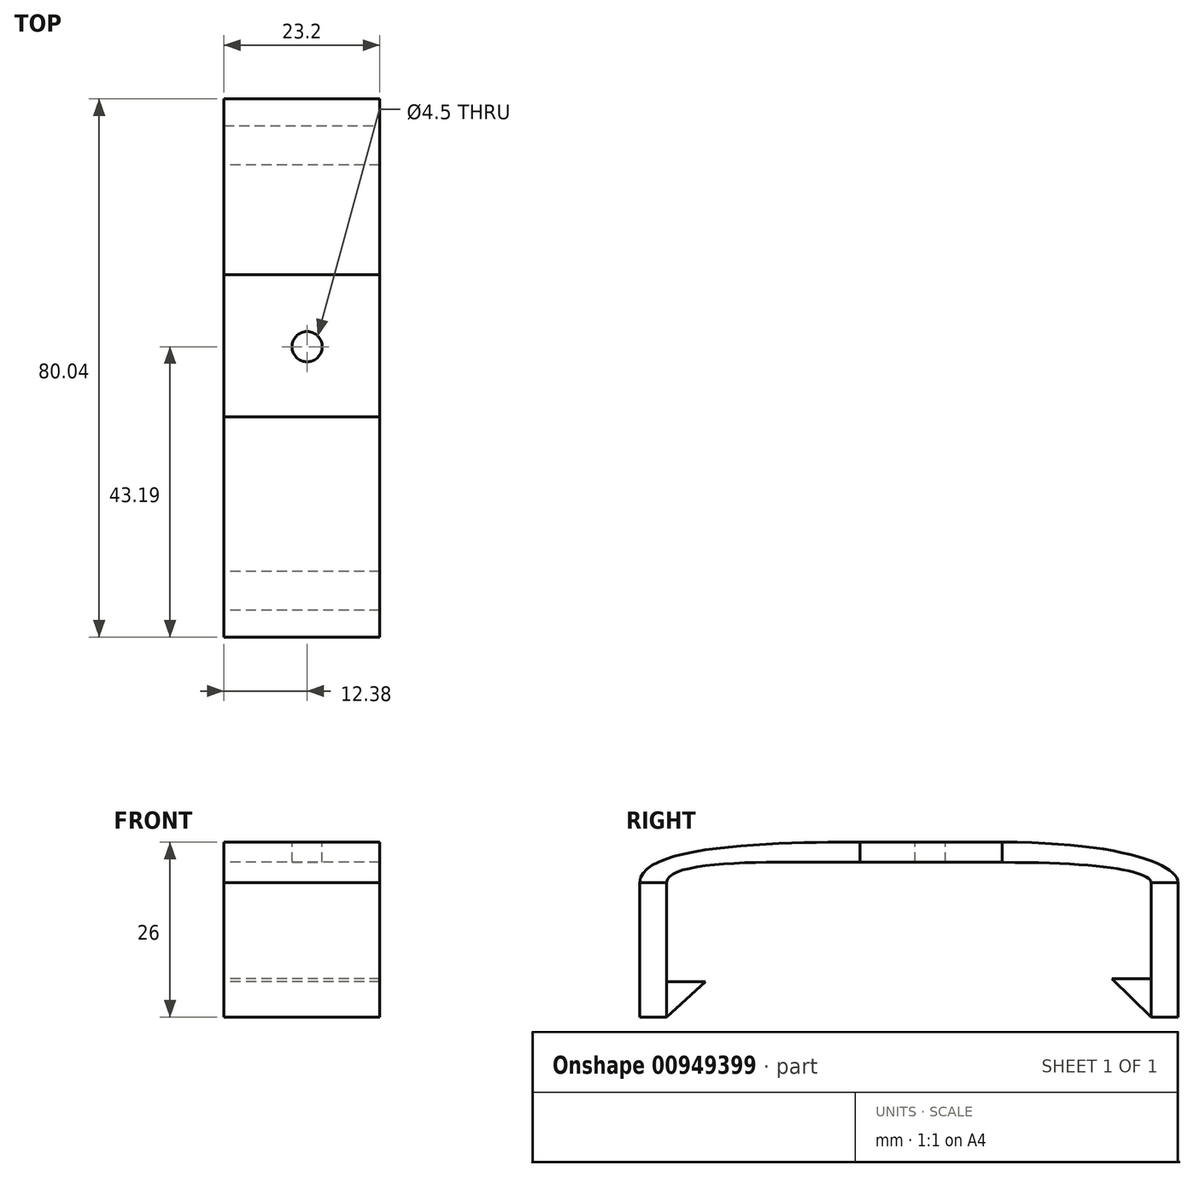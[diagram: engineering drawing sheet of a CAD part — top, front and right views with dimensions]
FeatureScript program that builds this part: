
annotation { "Feature Type Name" : "Feature", "Feature Type Description" : "" }
export const myFeature = defineFeature(function(context is Context, id is Id, definition is map)
    precondition{}
    {
        {
            var Q0;
            Q0=qCreatedBy(makeId("Top.planeOp"),FACE);
            var sketch = newSketch(context, id + "F0", { "sketchPlane" : qUnion([Q0])});
            skLineSegment(sketch, "E0.bottom", {"start": v(-12.38, 36.85) * mm, "end": v(10.8, 36.85) * mm});
            skLineSegment(sketch, "E0.top", {"start": v(-12.38, -43.19) * mm, "end": v(10.8, -43.19) * mm});
            skLineSegment(sketch, "E0.left", {"start": v(-12.38, 36.85) * mm, "end": v(-12.38, -43.19) * mm});
            skLineSegment(sketch, "E0.right", {"start": v(10.8, 36.85) * mm, "end": v(10.8, -43.19) * mm});
            skSolve(sketch);
        }
        {
            var Q0;
            Q0 = qSketchRegion(id + "F0", true);
            extrude(context, id + "F1", {"entities" : qUnion([Q0]), "depth" : 2 * mm, "offsetDistance" : 25 * mm});
        }
        {
            var Q0;
            Q0=makeQuery(id+"F1.opExtrude","CAP_FACE",FACE,{"disambiguationData":[OSD([sQuery(id+"F0.wireOp",EDGE,"E0.bottom"),sQuery(id+"F0.wireOp",EDGE,"E0.top"),sQuery(id+"F0.wireOp",EDGE,"E0.left"),sQuery(id+"F0.wireOp",EDGE,"E0.right")])],"isStart":false});
            var sketch = newSketch(context, id + "F2", { "sketchPlane" : qUnion([Q0])});
            skLineSegment(sketch, "E1.bottom", {"start": v(-12.38, 36.85) * mm, "end": v(10.8, 36.85) * mm});
            skLineSegment(sketch, "E1.top", {"start": v(-12.38, 32.85) * mm, "end": v(10.8, 32.85) * mm});
            skLineSegment(sketch, "E1.left", {"start": v(-12.38, 36.85) * mm, "end": v(-12.38, 32.85) * mm});
            skLineSegment(sketch, "E1.right", {"start": v(10.8, 36.85) * mm, "end": v(10.8, 32.85) * mm});
            skLineSegment(sketch, "E2.bottom", {"start": v(10.8, -43.19) * mm, "end": v(-12.38, -43.19) * mm});
            skLineSegment(sketch, "E2.top", {"start": v(10.8, -39.19) * mm, "end": v(-12.38, -39.19) * mm});
            skLineSegment(sketch, "E2.left", {"start": v(10.8, -43.19) * mm, "end": v(10.8, -39.19) * mm});
            skLineSegment(sketch, "E2.right", {"start": v(-12.38, -43.19) * mm, "end": v(-12.38, -39.19) * mm});
            skSolve(sketch);
        }
        {
            var Q0;
            Q0=makeQuery(id+"F2.imprint","IMPRINT",FACE,{"disambiguationData":[TD([[makeQuery(id+"F2.imprint","IMPRINT",EDGE,{"derivedFrom":sQuery(id+"F2.wireOp",EDGE,"E1.bottom")}),-1.0]])]});
            var Q1;
            Q1=makeQuery(id+"F2.imprint","IMPRINT",FACE,{"disambiguationData":[TD([[makeQuery(id+"F2.imprint","IMPRINT",EDGE,{"derivedFrom":sQuery(id+"F2.wireOp",EDGE,"E2.bottom")}),1.0]])]});
            extrude(context, id + "F3", {"entities" : qUnion([Q0, Q1]), "operationType" : NewBodyOperationType.ADD, "oppositeDirection" : true, "depth" : 22 * mm, "offsetDistance" : 25 * mm});
        }
        {
            var Q0;
            Q0=makeQuery(id+"F3.boolean.opBoolean","MERGE",FACE,{"derivedFrom":[makeQuery(id+"F1.opExtrude","SWEPT_FACE",FACE,{"disambiguationData":[OSD([sQuery(id+"F0.wireOp",EDGE,"E0.left")])]}),makeQuery(id+"F3.opExtrude","SWEPT_FACE",FACE,{"disambiguationData":[OSD([sQuery(id+"F2.wireOp",EDGE,"E1.left")])]}),makeQuery(id+"F3.opExtrude","SWEPT_FACE",FACE,{"disambiguationData":[OSD([sQuery(id+"F2.wireOp",EDGE,"E2.right")])]})]});
            var sketch = newSketch(context, id + "F4", { "sketchPlane" : qUnion([Q0])});
            skLineSegment(sketch, "E3", {"start": v(-32.85, -14.32) * mm, "end": v(-27.04, -14.32) * mm});
            skLineSegment(sketch, "E4", {"start": v(-27.04, -14.32) * mm, "end": v(-32.85, -20) * mm});
            skLineSegment(sketch, "E5", {"start": v(-32.85, -20) * mm, "end": v(-32.85, -14.32) * mm});
            skSolve(sketch);
        }
        {
            var Q0;
            Q0 = qSketchRegion(id + "F4", true);
            extrude(context, id + "F5", {"entities" : qUnion([Q0]), "operationType" : NewBodyOperationType.ADD, "oppositeDirection" : true, "depth" : 23.2 * mm, "offsetDistance" : 25 * mm});
        }
        {
            var Q0;
            Q0=makeQuery(id+"F5.boolean.opBoolean","MERGE",FACE,{"derivedFrom":[makeQuery(id+"F3.boolean.opBoolean","MERGE",FACE,{"derivedFrom":[makeQuery(id+"F1.opExtrude","SWEPT_FACE",FACE,{"disambiguationData":[OSD([sQuery(id+"F0.wireOp",EDGE,"E0.left")])]}),makeQuery(id+"F3.opExtrude","SWEPT_FACE",FACE,{"disambiguationData":[OSD([sQuery(id+"F2.wireOp",EDGE,"E1.left")])]}),makeQuery(id+"F3.opExtrude","SWEPT_FACE",FACE,{"disambiguationData":[OSD([sQuery(id+"F2.wireOp",EDGE,"E2.right")])]})]}),makeQuery(id+"F5.opExtrude","CAP_FACE",FACE,{"disambiguationData":[OSD([sQuery(id+"F4.wireOp",EDGE,"E3"),sQuery(id+"F4.wireOp",EDGE,"E4"),sQuery(id+"F4.wireOp",EDGE,"E5")])],"isStart":true})]});
            var sketch = newSketch(context, id + "F6", { "sketchPlane" : qUnion([Q0])});
            skLineSegment(sketch, "E6", {"start": v(39.19, -14.76) * mm, "end": v(33.44, -14.76) * mm});
            skLineSegment(sketch, "E7", {"start": v(33.44, -14.76) * mm, "end": v(39.19, -20) * mm});
            skLineSegment(sketch, "E8", {"start": v(39.19, -20) * mm, "end": v(39.19, -14.76) * mm});
            skSolve(sketch);
        }
        {
            var Q0;
            Q0 = qSketchRegion(id + "F6", true);
            extrude(context, id + "F7", {"entities" : qUnion([Q0]), "operationType" : NewBodyOperationType.ADD, "oppositeDirection" : true, "depth" : 23.2 * mm, "offsetDistance" : 25 * mm});
        }
        {
            var Q0;
            Q0=makeQuery(id+"F1.opExtrude","CAP_FACE",FACE,{"disambiguationData":[OSD([sQuery(id+"F0.wireOp",EDGE,"E0.bottom"),sQuery(id+"F0.wireOp",EDGE,"E0.top"),sQuery(id+"F0.wireOp",EDGE,"E0.left"),sQuery(id+"F0.wireOp",EDGE,"E0.right")])],"isStart":false});
            var sketch = newSketch(context, id + "F8", { "sketchPlane" : qUnion([Q0])});
            skCircle(sketch, "E9", {"center": v(0, 0) * mm, "radius": 2.25 * mm});
            skSolve(sketch);
        }
        {
            var Q0;
            Q0 = qSketchRegion(id + "F8", true);
            extrude(context, id + "F9", {"entities" : qUnion([Q0]), "operationType" : NewBodyOperationType.REMOVE, "oppositeDirection" : true, "depth" : 25 * mm, "offsetDistance" : 25 * mm});
        }
        {
            var Q0;
            Q0=makeQuery(id+"F1.opExtrude","CAP_FACE",FACE,{"disambiguationData":[OSD([sQuery(id+"F0.wireOp",EDGE,"E0.bottom"),sQuery(id+"F0.wireOp",EDGE,"E0.top"),sQuery(id+"F0.wireOp",EDGE,"E0.left"),sQuery(id+"F0.wireOp",EDGE,"E0.right")])],"isStart":true});
            var sketch = newSketch(context, id + "F10", { "sketchPlane" : qUnion([Q0])});
            skLineSegment(sketch, "E10.bottom", {"start": v(10.8, 10.41) * mm, "end": v(-12.38, 10.41) * mm});
            skLineSegment(sketch, "E10.top", {"start": v(10.8, -10.7) * mm, "end": v(-12.38, -10.7) * mm});
            skLineSegment(sketch, "E10.left", {"start": v(10.8, 10.41) * mm, "end": v(10.8, -10.7) * mm});
            skLineSegment(sketch, "E10.right", {"start": v(-12.38, 10.41) * mm, "end": v(-12.38, -10.7) * mm});
            skSolve(sketch);
        }
        {
            var Q0;
            Q0=makeQuery(id+"F10.imprint","IMPRINT",FACE,{"disambiguationData":[TD([[makeQuery(id+"F10.imprint","IMPRINT",EDGE,{"derivedFrom":sQuery(id+"F10.wireOp",EDGE,"E10.bottom")}),1.0]])]});
            extrude(context, id + "F11", {"entities" : qUnion([Q0]), "operationType" : NewBodyOperationType.ADD, "oppositeDirection" : true, "depth" : 6 * mm, "offsetDistance" : 25 * mm});
        }
        {
            var Q0;
            Q0 = qSketchRegion(id + "F10", true);
            extrude(context, id + "F12", {"entities" : qUnion([Q0]), "operationType" : NewBodyOperationType.REMOVE, "oppositeDirection" : true, "depth" : 3 * mm, "offsetDistance" : 25 * mm});
        }
        {
            var Q0;
            Q0 = qSketchRegion(id + "F0", true);
            extrude(context, id + "F13", {"entities" : qUnion([Q0]), "operationType" : NewBodyOperationType.REMOVE, "depth" : 3 * mm, "offsetDistance" : 25 * mm});
        }
        {
            var Q0;
            Q0=makeQuery(id+"F11.opExtrude","SWEPT_FACE",FACE,{"disambiguationData":[OSD([sQuery(id+"F10.wireOp",EDGE,"E10.bottom")])]});
            var Q1;
            {var subQ0=sQuery(id+"F0.wireOp",EDGE,"E0.top");var subQ1=sQuery(id+"F0.wireOp",EDGE,"E0.left");var subQ2=sQuery(id+"F0.wireOp",EDGE,"E0.right");Q1=makeQuery(id+"F13.boolean.opBoolean","COPY",FACE,{"disambiguationData":[TD([makeQuery(id+"F1.opExtrude","SWEPT_FACE",FACE,{"disambiguationData":[OSD([subQ0])]})])],"derivedFrom":makeQuery(id+"F13.opExtrude","CAP_FACE",FACE,{"disambiguationData":[OSD([sQuery(id+"F0.wireOp",EDGE,"E0.bottom"),subQ0,subQ1,subQ2])],"isStart":true})});}
            loft(context, id + "F14", {"startCondition" : LoftEndDerivativeType.NORMAL_TO_PROFILE, "startMagnitude" : 1, "endCondition" : LoftEndDerivativeType.NORMAL_TO_PROFILE, "endMagnitude" : 2, "sheetProfilesArray" : [{ "sheetProfileEntities" : qUnion([Q0]) }, { "sheetProfileEntities" : qUnion([Q1]) }]});
        }
        {
            var Q0;
            {var subQ0=sQuery(id+"F0.wireOp",EDGE,"E0.bottom");var subQ1=sQuery(id+"F0.wireOp",EDGE,"E0.right");var subQ2=sQuery(id+"F0.wireOp",EDGE,"E0.left");Q0=makeQuery(id+"F13.boolean.opBoolean","COPY",FACE,{"disambiguationData":[TD([makeQuery(id+"F1.opExtrude","SWEPT_FACE",FACE,{"disambiguationData":[OSD([subQ0])]})])],"derivedFrom":makeQuery(id+"F13.opExtrude","CAP_FACE",FACE,{"disambiguationData":[OSD([subQ0,sQuery(id+"F0.wireOp",EDGE,"E0.top"),subQ2,subQ1])],"isStart":true})});}
            var Q1;
            Q1=makeQuery(id+"F11.opExtrude","SWEPT_FACE",FACE,{"disambiguationData":[OSD([sQuery(id+"F10.wireOp",EDGE,"E10.top")])]});
            loft(context, id + "F15", {"startCondition" : LoftEndDerivativeType.NORMAL_TO_PROFILE, "startMagnitude" : 1, "endCondition" : LoftEndDerivativeType.NORMAL_TO_PROFILE, "endMagnitude" : 2, "sheetProfilesArray" : [{ "sheetProfileEntities" : qUnion([Q0]) }, { "sheetProfileEntities" : qUnion([Q1]) }]});
        }
    });
